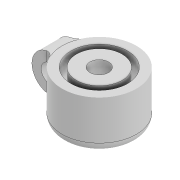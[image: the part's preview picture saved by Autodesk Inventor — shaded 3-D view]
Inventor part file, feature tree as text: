
AUTODESK INVENTOR PART (.ipt)
format: ipt  version: 2022 (Build 260153000, 153)  size: 167,936 bytes
history: native  units: mm
features: extrude x3, sketch x3, projected_geometry x2, fillet x1
ambient origin geometry x8: Origin, YZ Plane, XZ Plane, XY Plane, X Axis, Y Axis, Z Axis, Center Point
bodies: Solid1 (feature_tree)
feature tree (9):
  extrude  "Extrusion1"  Depth=2.5mm TaperAngle=0.0deg
  extrude  "Extrusion2"  Depth=12.2mm
  extrude  "Extrusion3"  Depth=2.0mm
  fillet  "Fillet2"  Radius=5.0mm
  sketch  "Sketch1"  dims[d0=16.0mm d1=2.5mm d2=0.0mm]
  sketch  "Sketch2"  dims[d3=9.8mm d4=12.2mm]
  projected_geometry  "Projected Loop1"
  sketch  "Sketch3"  dims[d5=8.0mm d6=0.0mm d8=4.0mm d11=5.0mm d12=0.0mm d14=4.0mm d15=2.0mm d16=4.0mm d17=2.0mm]
  projected_geometry  "Projected Loop2"
